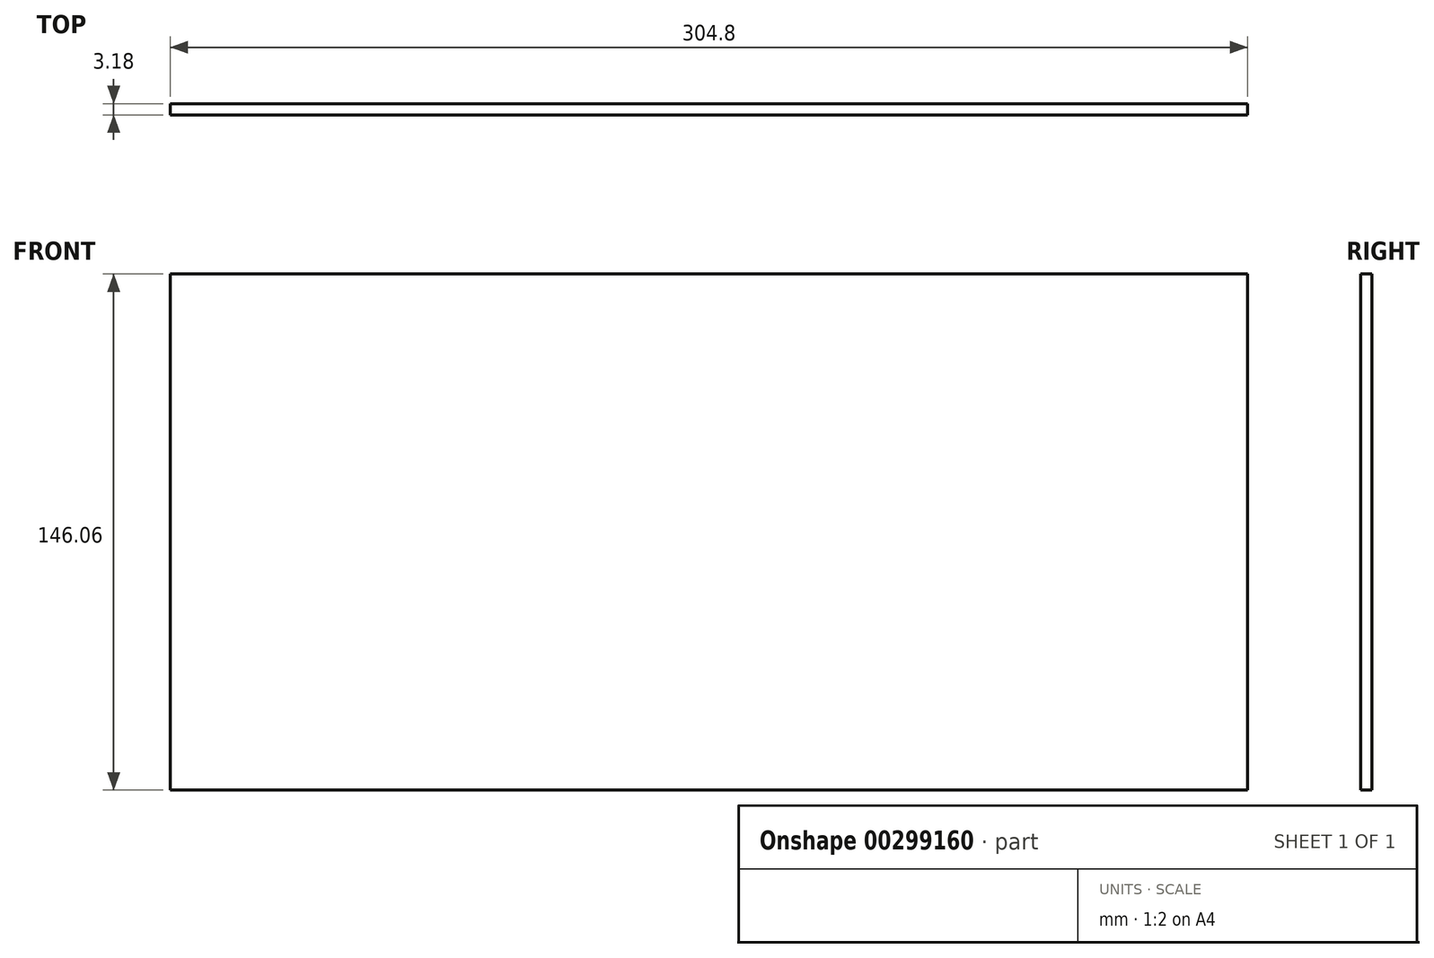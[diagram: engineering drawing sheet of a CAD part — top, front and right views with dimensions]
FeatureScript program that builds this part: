
annotation { "Feature Type Name" : "Feature", "Feature Type Description" : "" }
export const myFeature = defineFeature(function(context is Context, id is Id, definition is map)
    precondition{}
    {
        {
            var Q0;
            Q0=qCreatedBy(makeId("Front.planeOp"),FACE);
            var sketch = newSketch(context, id + "F0", { "sketchPlane" : qUnion([Q0])});
            skLineSegment(sketch, "E0.bottom", {"start": v(-152.4, 73.03) * mm, "end": v(152.4, 73.03) * mm});
            skLineSegment(sketch, "E0.top", {"start": v(-152.4, -73.03) * mm, "end": v(152.4, -73.03) * mm});
            skLineSegment(sketch, "E0.left", {"start": v(-152.4, 73.03) * mm, "end": v(-152.4, -73.03) * mm});
            skLineSegment(sketch, "E0.right", {"start": v(152.4, 73.03) * mm, "end": v(152.4, -73.03) * mm});
            skPoint(sketch, "E0.middle", {"position": v(0, 0) * mm});
            skSolve(sketch);
        }
        {
            var Q0;
            Q0 = qSketchRegion(id + "F0", true);
            extrude(context, id + "F1", {"entities" : qUnion([Q0]), "endBound" : BoundingType.SYMMETRIC, "depth" : 3.17 * mm});
        }
    });
